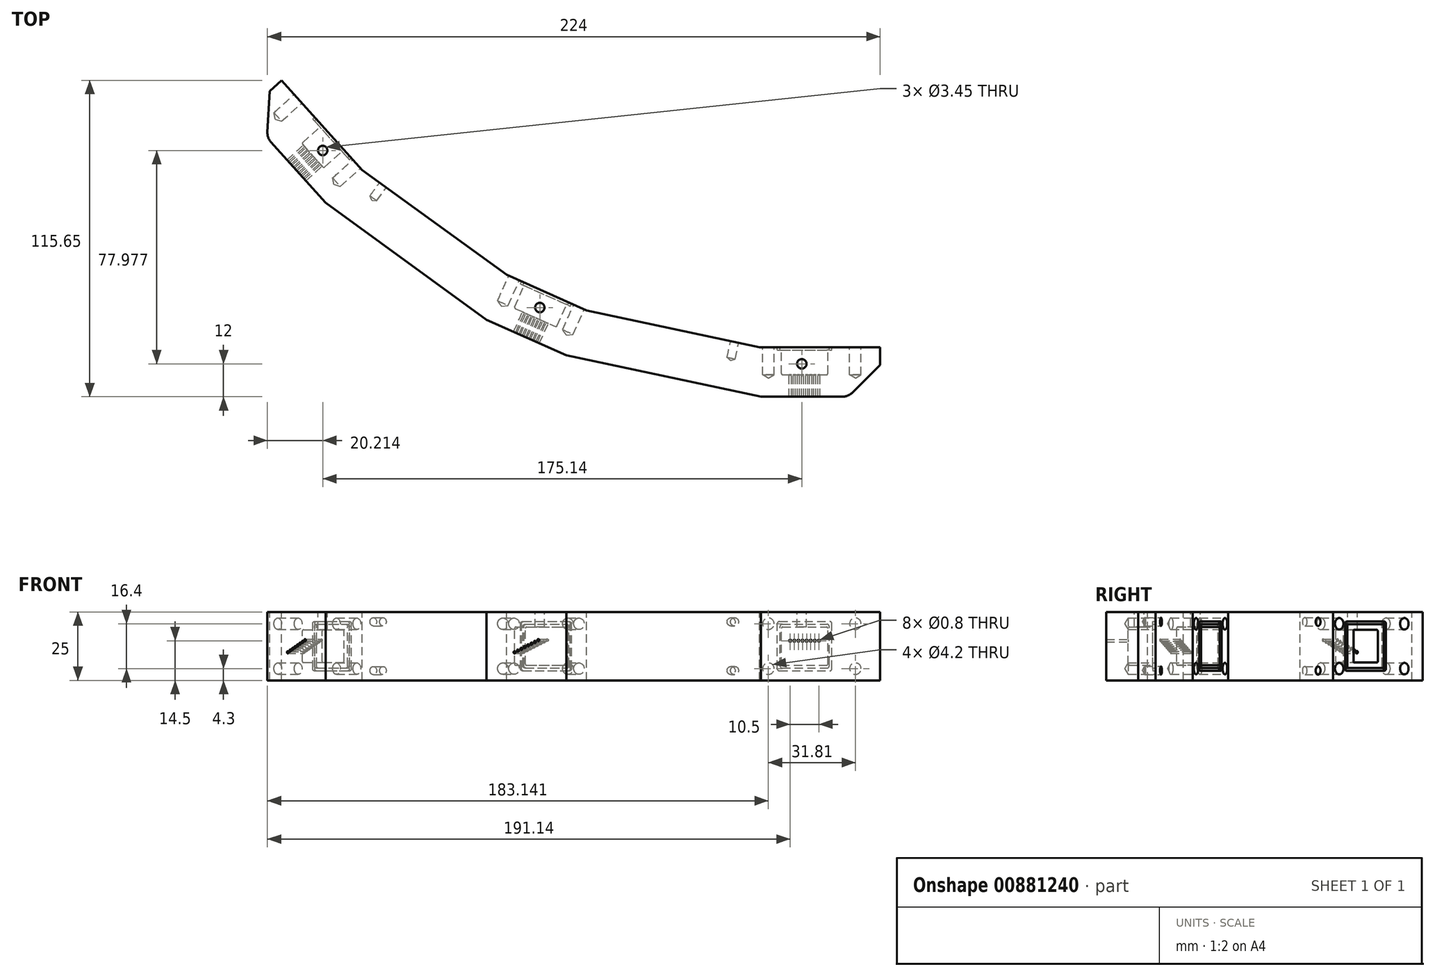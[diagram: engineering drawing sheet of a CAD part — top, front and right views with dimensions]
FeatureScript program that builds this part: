
annotation { "Feature Type Name" : "Feature", "Feature Type Description" : "" }
export const myFeature = defineFeature(function(context is Context, id is Id, definition is map)
    precondition{}
    {
        {
            var Q0;
            Q0=qCreatedBy(makeId("Top.planeOp"),FACE);
            var sketch = newSketch(context, id + "F0", { "sketchPlane" : qUnion([Q0])});
            skCircle(sketch, "E0", {"center": v(0, -260) * mm, "radius": 6 * mm});
            skCircle(sketch, "E1", {"center": v(-105.75, -237.52) * mm, "radius": 6 * mm});
            skCircle(sketch, "E2", {"center": v(-193.22, -173.97) * mm, "radius": 6 * mm});
            skPoint(sketch, "E3", {"position": v(-185.79, -167.28) * mm});
            skPoint(sketch, "E4", {"position": v(-101.68, -228.39) * mm});
            skPoint(sketch, "E5", {"position": v(0, -250) * mm});
            skLineSegment(sketch, "E6.trimOffspring", {"start": v(-103.31, -232.04) * mm, "end": v(-105.75, -237.52) * mm});
            skLineSegment(sketch, "E7.trimOffspring", {"start": v(0, -254) * mm, "end": v(0, -260) * mm});
            skLineSegment(sketch, "E8.trimOffspring", {"start": v(-188.76, -169.96) * mm, "end": v(-193.22, -173.97) * mm});
            skLineSegment(sketch, "E9", {"start": v(-185.79, -167.28) * mm, "end": v(-175.08, -179.17) * mm});
            skLineSegment(sketch, "E10", {"start": v(-185.79, -167.28) * mm, "end": v(-195.1, -156.93) * mm});
            skLineSegment(sketch, "E11", {"start": v(-101.68, -228.39) * mm, "end": v(-116.3, -221.88) * mm});
            skLineSegment(sketch, "E12", {"start": v(-101.68, -228.39) * mm, "end": v(-87.07, -234.9) * mm});
            skLineSegment(sketch, "E13", {"start": v(0, -250) * mm, "end": v(-16, -250) * mm});
            skLineSegment(sketch, "E14", {"start": v(0, -250) * mm, "end": v(13.93, -250) * mm});
            skLineSegment(sketch, "E15", {"start": v(-175.08, -179.17) * mm, "end": v(-116.3, -221.88) * mm});
            skLineSegment(sketch, "E16", {"start": v(-87.07, -234.9) * mm, "end": v(-16, -250) * mm});
            skLineSegment(sketch, "E17", {"start": v(-196.38, -153.32) * mm, "end": v(-195.6, -138.3) * mm});
            skLineSegment(sketch, "E18", {"start": v(17.46, -248.54) * mm, "end": v(27.61, -238.39) * mm});
            skPoint(sketch, "E19", {"position": v(-196.5, -155.4) * mm});
            skPoint(sketch, "E20", {"position": v(-172.4, -155.24) * mm});
            skLineSegment(sketch, "E21", {"start": v(-172.4, -155.24) * mm, "end": v(-191.22, -134.35) * mm});
            skLineSegment(sketch, "E22", {"start": v(-195.6, -138.3) * mm, "end": v(-191.22, -134.35) * mm});
            skPoint(sketch, "E23", {"position": v(-94.36, -211.94) * mm});
            skLineSegment(sketch, "E24", {"start": v(-94.36, -211.94) * mm, "end": v(-108.98, -205.43) * mm});
            skLineSegment(sketch, "E25", {"start": v(-172.4, -155.24) * mm, "end": v(-161.7, -167.13) * mm});
            skLineSegment(sketch, "E26", {"start": v(-161.7, -167.13) * mm, "end": v(-108.98, -205.43) * mm});
            skLineSegment(sketch, "E27", {"start": v(-94.36, -211.94) * mm, "end": v(-79.75, -218.45) * mm});
            skPoint(sketch, "E28", {"position": v(-0.5, -232) * mm});
            skLineSegment(sketch, "E29", {"start": v(-0.5, -232) * mm, "end": v(27.61, -232) * mm});
            skLineSegment(sketch, "E30", {"start": v(27.61, -238.39) * mm, "end": v(27.61, -232) * mm});
            skLineSegment(sketch, "E31", {"start": v(-0.5, -232) * mm, "end": v(-16.5, -232) * mm});
            skLineSegment(sketch, "E32", {"start": v(-79.75, -218.45) * mm, "end": v(-16.5, -232) * mm});
            skPoint(sketch, "E33.start.orphan", {"position": v(0, 0) * mm});
            skArc(sketch, "E34.filletArc", {"start": v(-196.38, -153.32) * mm, "mid": v(-196.1, -155.25) * mm, "end": v(-195.1, -156.93) * mm});
            skPoint(sketch, "E35.visualSharp", {"position": v(16, -250) * mm});
            skArc(sketch, "E35.filletArc", {"start": v(13.93, -250) * mm, "mid": v(15.84, -249.62) * mm, "end": v(17.46, -248.54) * mm});
            skSolve(sketch);
        }
        {
            var Q0;
            Q0=makeQuery(id+"F0.imprint","IMPRINT",FACE,{"disambiguationData":[TD([[makeQuery(id+"F0.imprint","IMPRINT",EDGE,{"derivedFrom":sQuery(id+"F0.wireOp",EDGE,"E9")}),1.0]])]});
            extrude(context, id + "F1", {"entities" : qUnion([Q0]), "oppositeDirection" : true, "depth" : 25 * mm, "offsetDistance" : 25 * mm});
        }
        {
            var Q0;
            Q0=makeQuery(id+"F1.opExtrude","SWEPT_FACE",FACE,{"disambiguationData":[OSD([sQuery(id+"F0.wireOp",EDGE,"E24"),sQuery(id+"F0.wireOp",EDGE,"E27")])]});
            var sketch = newSketch(context, id + "F2", { "sketchPlane" : qUnion([Q0])});
            skPoint(sketch, "E36", {"position": v(0, -12.5) * mm});
            skLineSegment(sketch, "E37.bottom", {"start": v(8.5, -19.5) * mm, "end": v(-8.5, -19.5) * mm});
            skLineSegment(sketch, "E37.top", {"start": v(8.5, -5.5) * mm, "end": v(-8.5, -5.5) * mm});
            skLineSegment(sketch, "E37.left", {"start": v(8.5, -19.5) * mm, "end": v(8.5, -5.5) * mm});
            skLineSegment(sketch, "E37.right", {"start": v(-8.5, -19.5) * mm, "end": v(-8.5, -5.5) * mm});
            skSolve(sketch);
        }
        {
            var Q0;
            Q0=makeQuery(id+"F2.imprint","IMPRINT",FACE,{"disambiguationData":[TD([[makeQuery(id+"F2.imprint","IMPRINT",EDGE,{"derivedFrom":sQuery(id+"F2.wireOp",EDGE,"E37.bottom")}),-1.0]])]});
            extrude(context, id + "F3", {"entities" : qUnion([Q0]), "operationType" : NewBodyOperationType.REMOVE, "oppositeDirection" : true, "depth" : 10 * mm, "offsetDistance" : 25 * mm});
        }
        {
            var Q0;
            Q0=makeQuery(id+"F1.opExtrude","SWEPT_FACE",FACE,{"disambiguationData":[OSD([sQuery(id+"F0.wireOp",EDGE,"E21"),sQuery(id+"F0.wireOp",EDGE,"E25")])]});
            var sketch = newSketch(context, id + "F4", { "sketchPlane" : qUnion([Q0])});
            skPoint(sketch, "E38.middle", {"position": v(0, -12.5) * mm});
            skLineSegment(sketch, "E39.bottom", {"start": v(6, -18.5) * mm, "end": v(-6, -18.5) * mm});
            skLineSegment(sketch, "E39.top", {"start": v(6, -6.5) * mm, "end": v(-6, -6.5) * mm});
            skLineSegment(sketch, "E39.left", {"start": v(6, -18.5) * mm, "end": v(6, -6.5) * mm});
            skLineSegment(sketch, "E39.right", {"start": v(-6, -18.5) * mm, "end": v(-6, -6.5) * mm});
            skSolve(sketch);
        }
        {
            var Q0;
            Q0=makeQuery(id+"F4.imprint","IMPRINT",FACE,{"disambiguationData":[TD([[makeQuery(id+"F4.imprint","IMPRINT",EDGE,{"derivedFrom":sQuery(id+"F4.wireOp",EDGE,"E39.bottom")}),-1.0]])]});
            extrude(context, id + "F5", {"entities" : qUnion([Q0]), "operationType" : NewBodyOperationType.REMOVE, "oppositeDirection" : true, "depth" : 10 * mm, "offsetDistance" : 25 * mm});
        }
        {
            var Q0;
            Q0=makeQuery(id+"F5.boolean.opBoolean","COPY",FACE,{"derivedFrom":makeQuery(id+"F5.opExtrude","CAP_FACE",FACE,{"disambiguationData":[OSD([sQuery(id+"F4.wireOp",EDGE,"E39.bottom"),sQuery(id+"F4.wireOp",EDGE,"E39.top"),sQuery(id+"F4.wireOp",EDGE,"E39.left"),sQuery(id+"F4.wireOp",EDGE,"E39.right")])],"isStart":false})});
            var sketch = newSketch(context, id + "F6", { "sketchPlane" : qUnion([Q0])});
            skLineSegment(sketch, "E40", {"start": v(0, -18.5) * mm, "end": v(0, -12.5) * mm});
            skLineSegment(sketch, "E41", {"start": v(0, -12.5) * mm, "end": v(6.8, -15.67) * mm});
            skLineSegment(sketch, "E42", {"start": v(0, -12.5) * mm, "end": v(-6.8, -9.33) * mm});
            skPoint(sketch, "E43", {"position": v(0.68, -12.82) * mm});
            skPoint(sketch, "E44", {"position": v(2.04, -13.45) * mm});
            skPoint(sketch, "E45", {"position": v(3.4, -14.08) * mm});
            skPoint(sketch, "E46", {"position": v(4.76, -14.72) * mm});
            skPoint(sketch, "E47", {"position": v(-0.68, -12.18) * mm});
            skPoint(sketch, "E48", {"position": v(-2.04, -11.55) * mm});
            skPoint(sketch, "E49", {"position": v(-3.4, -10.92) * mm});
            skPoint(sketch, "E50", {"position": v(-4.76, -10.28) * mm});
            skSolve(sketch);
        }
        {
            var Q0;
            Q0=sQuery(id+"F6.wireOp",VERTEX,"E46");
            var Q1;
            Q1=sQuery(id+"F6.wireOp",VERTEX,"E45");
            var Q2;
            Q2=sQuery(id+"F6.wireOp",VERTEX,"E44");
            var Q3;
            Q3=sQuery(id+"F6.wireOp",VERTEX,"E43");
            var Q4;
            Q4=sQuery(id+"F6.wireOp",VERTEX,"E47");
            var Q5;
            Q5=sQuery(id+"F6.wireOp",VERTEX,"E48");
            var Q6;
            Q6=sQuery(id+"F6.wireOp",VERTEX,"E49");
            var Q7;
            Q7=sQuery(id+"F6.wireOp",VERTEX,"E50");
            var Q8;
            Q8=makeQuery(id+"F1.opExtrude","SWEPT_BODY",BODY,{"disambiguationData":[OSD([sQuery(id+"F0.wireOp",EDGE,"E9"),sQuery(id+"F0.wireOp",EDGE,"E10"),sQuery(id+"F0.wireOp",EDGE,"E11"),sQuery(id+"F0.wireOp",EDGE,"E12"),sQuery(id+"F0.wireOp",EDGE,"E13"),sQuery(id+"F0.wireOp",EDGE,"E14"),sQuery(id+"F0.wireOp",EDGE,"E15"),sQuery(id+"F0.wireOp",EDGE,"E16"),sQuery(id+"F0.wireOp",EDGE,"E17"),sQuery(id+"F0.wireOp",EDGE,"E18"),sQuery(id+"F0.wireOp",EDGE,"E21"),sQuery(id+"F0.wireOp",EDGE,"E22"),sQuery(id+"F0.wireOp",EDGE,"E24"),sQuery(id+"F0.wireOp",EDGE,"E25"),sQuery(id+"F0.wireOp",EDGE,"E26"),sQuery(id+"F0.wireOp",EDGE,"E27"),sQuery(id+"F0.wireOp",EDGE,"E29"),sQuery(id+"F0.wireOp",EDGE,"E30"),sQuery(id+"F0.wireOp",EDGE,"E31"),sQuery(id+"F0.wireOp",EDGE,"E32"),sQuery(id+"F0.wireOp",EDGE,"E34.filletArc"),sQuery(id+"F0.wireOp",EDGE,"E35.filletArc")])]});
            hole(context, id + "F7", {"style" : HoleStyle.C_SINK, "endStyle" : HoleEndStyle.THROUGH, "holeDiameter" : 0.8 * mm, "cSinkDiameter" : 0.87 * mm, "cSinkAngle" : 60 * degree, "majorDiameter" : 5 * mm, "isTappedThrough" : true, "tappedDepth" : 12 * mm, "tapClearance" : 3, "locations" : qUnion([Q0, Q1, Q2, Q3, Q4, Q5, Q6, Q7]), "scope" : qUnion([Q8])});
        }
        {
            var Q0;
            Q0=makeQuery(id+"F3.boolean.opBoolean","COPY",FACE,{"derivedFrom":makeQuery(id+"F3.opExtrude","CAP_FACE",FACE,{"disambiguationData":[OSD([sQuery(id+"F2.wireOp",EDGE,"E37.bottom"),sQuery(id+"F2.wireOp",EDGE,"E37.top"),sQuery(id+"F2.wireOp",EDGE,"E37.left"),sQuery(id+"F2.wireOp",EDGE,"E37.right")])],"isStart":false})});
            var sketch = newSketch(context, id + "F8", { "sketchPlane" : qUnion([Q0])});
            skLineSegment(sketch, "E51", {"start": v(0, -19.5) * mm, "end": v(0, -12.5) * mm});
            skLineSegment(sketch, "E52", {"start": v(0, -12.5) * mm, "end": v(5.15, -14.9) * mm});
            skLineSegment(sketch, "E53", {"start": v(0, -12.5) * mm, "end": v(-6.8, -9.33) * mm});
            skPoint(sketch, "E54", {"position": v(0.68, -12.82) * mm});
            skPoint(sketch, "E55", {"position": v(2.04, -13.45) * mm});
            skPoint(sketch, "E56", {"position": v(3.4, -14.08) * mm});
            skPoint(sketch, "E57", {"position": v(-0.68, -12.18) * mm});
            skPoint(sketch, "E58", {"position": v(-2.04, -11.55) * mm});
            skPoint(sketch, "E59", {"position": v(-3.4, -10.92) * mm});
            skPoint(sketch, "E60", {"position": v(4.76, -14.72) * mm});
            skPoint(sketch, "E61", {"position": v(-4.76, -10.28) * mm});
            skSolve(sketch);
        }
        {
            var Q0;
            Q0=sQuery(id+"F8.wireOp",VERTEX,"E60");
            var Q1;
            Q1=sQuery(id+"F8.wireOp",VERTEX,"E56");
            var Q2;
            Q2=sQuery(id+"F8.wireOp",VERTEX,"E55");
            var Q3;
            Q3=sQuery(id+"F8.wireOp",VERTEX,"E54");
            var Q4;
            Q4=sQuery(id+"F8.wireOp",VERTEX,"E57");
            var Q5;
            Q5=sQuery(id+"F8.wireOp",VERTEX,"E58");
            var Q6;
            Q6=sQuery(id+"F8.wireOp",VERTEX,"E59");
            var Q7;
            Q7=sQuery(id+"F8.wireOp",VERTEX,"E61");
            var Q8;
            Q8=makeQuery(id+"F1.opExtrude","SWEPT_BODY",BODY,{"disambiguationData":[OSD([sQuery(id+"F0.wireOp",EDGE,"E9"),sQuery(id+"F0.wireOp",EDGE,"E10"),sQuery(id+"F0.wireOp",EDGE,"E11"),sQuery(id+"F0.wireOp",EDGE,"E12"),sQuery(id+"F0.wireOp",EDGE,"E13"),sQuery(id+"F0.wireOp",EDGE,"E14"),sQuery(id+"F0.wireOp",EDGE,"E15"),sQuery(id+"F0.wireOp",EDGE,"E16"),sQuery(id+"F0.wireOp",EDGE,"E17"),sQuery(id+"F0.wireOp",EDGE,"E18"),sQuery(id+"F0.wireOp",EDGE,"E21"),sQuery(id+"F0.wireOp",EDGE,"E22"),sQuery(id+"F0.wireOp",EDGE,"E24"),sQuery(id+"F0.wireOp",EDGE,"E25"),sQuery(id+"F0.wireOp",EDGE,"E26"),sQuery(id+"F0.wireOp",EDGE,"E27"),sQuery(id+"F0.wireOp",EDGE,"E29"),sQuery(id+"F0.wireOp",EDGE,"E30"),sQuery(id+"F0.wireOp",EDGE,"E31"),sQuery(id+"F0.wireOp",EDGE,"E32"),sQuery(id+"F0.wireOp",EDGE,"E34.filletArc"),sQuery(id+"F0.wireOp",EDGE,"E35.filletArc")])]});
            hole(context, id + "F9", {"style" : HoleStyle.C_SINK, "endStyle" : HoleEndStyle.THROUGH, "holeDiameter" : 0.8 * mm, "cSinkDiameter" : 0.87 * mm, "cSinkAngle" : 60 * degree, "majorDiameter" : 5 * mm, "isTappedThrough" : true, "tappedDepth" : 12 * mm, "tapClearance" : 3, "locations" : qUnion([Q0, Q1, Q2, Q3, Q4, Q5, Q6, Q7]), "scope" : qUnion([Q8])});
        }
        {
            var Q0;
            Q0=makeQuery(id+"F1.opExtrude","SWEPT_FACE",FACE,{"disambiguationData":[OSD([sQuery(id+"F0.wireOp",EDGE,"E29"),sQuery(id+"F0.wireOp",EDGE,"E31")])]});
            var sketch = newSketch(context, id + "F10", { "sketchPlane" : qUnion([Q0])});
            skLineSegment(sketch, "E62.bottom", {"start": v(8.5, -19.5) * mm, "end": v(-8.5, -19.5) * mm});
            skLineSegment(sketch, "E62.top", {"start": v(8.5, -5.5) * mm, "end": v(-8.5, -5.5) * mm});
            skLineSegment(sketch, "E62.left", {"start": v(8.5, -19.5) * mm, "end": v(8.5, -5.5) * mm});
            skLineSegment(sketch, "E62.right", {"start": v(-8.5, -19.5) * mm, "end": v(-8.5, -5.5) * mm});
            skPoint(sketch, "E62.middle", {"position": v(0, -12.5) * mm});
            skSolve(sketch);
        }
        {
            var Q0;
            Q0=makeQuery(id+"F10.imprint","IMPRINT",FACE,{"disambiguationData":[TD([[makeQuery(id+"F10.imprint","IMPRINT",EDGE,{"derivedFrom":sQuery(id+"F10.wireOp",EDGE,"E62.bottom")}),-1.0]])]});
            extrude(context, id + "F11", {"entities" : qUnion([Q0]), "operationType" : NewBodyOperationType.REMOVE, "oppositeDirection" : true, "depth" : 10 * mm, "offsetDistance" : 25 * mm});
        }
        {
            var Q0;
            Q0=makeQuery(id+"F11.boolean.opBoolean","COPY",FACE,{"derivedFrom":makeQuery(id+"F11.opExtrude","CAP_FACE",FACE,{"disambiguationData":[OSD([sQuery(id+"F10.wireOp",EDGE,"E62.bottom"),sQuery(id+"F10.wireOp",EDGE,"E62.top"),sQuery(id+"F10.wireOp",EDGE,"E62.left"),sQuery(id+"F10.wireOp",EDGE,"E62.right")])],"isStart":false})});
            var sketch = newSketch(context, id + "F12", { "sketchPlane" : qUnion([Q0])});
            skLineSegment(sketch, "E63", {"start": v(0, -19.5) * mm, "end": v(0, -10.5) * mm});
            skPoint(sketch, "E64", {"position": v(0.75, -10.5) * mm});
            skPoint(sketch, "E65", {"position": v(2.25, -10.5) * mm});
            skPoint(sketch, "E66", {"position": v(3.75, -10.5) * mm});
            skPoint(sketch, "E67", {"position": v(5.25, -10.5) * mm});
            skPoint(sketch, "E68", {"position": v(-0.75, -10.5) * mm});
            skPoint(sketch, "E69", {"position": v(-2.25, -10.5) * mm});
            skPoint(sketch, "E70", {"position": v(-3.75, -10.5) * mm});
            skPoint(sketch, "E71", {"position": v(-5.25, -10.5) * mm});
            skSolve(sketch);
        }
        {
            var Q0;
            Q0=sQuery(id+"F12.wireOp",VERTEX,"E67");
            var Q1;
            Q1=sQuery(id+"F12.wireOp",VERTEX,"E66");
            var Q2;
            Q2=sQuery(id+"F12.wireOp",VERTEX,"E65");
            var Q3;
            Q3=sQuery(id+"F12.wireOp",VERTEX,"E64");
            var Q4;
            Q4=sQuery(id+"F12.wireOp",VERTEX,"E68");
            var Q5;
            Q5=sQuery(id+"F12.wireOp",VERTEX,"E69");
            var Q6;
            Q6=sQuery(id+"F12.wireOp",VERTEX,"E70");
            var Q7;
            Q7=sQuery(id+"F12.wireOp",VERTEX,"E71");
            var Q8;
            Q8=makeQuery(id+"F1.opExtrude","SWEPT_BODY",BODY,{"disambiguationData":[OSD([sQuery(id+"F0.wireOp",EDGE,"E9"),sQuery(id+"F0.wireOp",EDGE,"E10"),sQuery(id+"F0.wireOp",EDGE,"E11"),sQuery(id+"F0.wireOp",EDGE,"E12"),sQuery(id+"F0.wireOp",EDGE,"E13"),sQuery(id+"F0.wireOp",EDGE,"E14"),sQuery(id+"F0.wireOp",EDGE,"E15"),sQuery(id+"F0.wireOp",EDGE,"E16"),sQuery(id+"F0.wireOp",EDGE,"E17"),sQuery(id+"F0.wireOp",EDGE,"E18"),sQuery(id+"F0.wireOp",EDGE,"E21"),sQuery(id+"F0.wireOp",EDGE,"E22"),sQuery(id+"F0.wireOp",EDGE,"E24"),sQuery(id+"F0.wireOp",EDGE,"E25"),sQuery(id+"F0.wireOp",EDGE,"E26"),sQuery(id+"F0.wireOp",EDGE,"E27"),sQuery(id+"F0.wireOp",EDGE,"E29"),sQuery(id+"F0.wireOp",EDGE,"E30"),sQuery(id+"F0.wireOp",EDGE,"E31"),sQuery(id+"F0.wireOp",EDGE,"E32"),sQuery(id+"F0.wireOp",EDGE,"E34.filletArc"),sQuery(id+"F0.wireOp",EDGE,"E35.filletArc")])]});
            hole(context, id + "F13", {"style" : HoleStyle.C_SINK, "endStyle" : HoleEndStyle.THROUGH, "holeDiameter" : 0.8 * mm, "cSinkDiameter" : 0.87 * mm, "cSinkAngle" : 60 * degree, "majorDiameter" : 5 * mm, "isTappedThrough" : true, "tappedDepth" : 12 * mm, "tapClearance" : 3, "locations" : qUnion([Q0, Q1, Q2, Q3, Q4, Q5, Q6, Q7]), "scope" : qUnion([Q8])});
        }
        {
            var Q0;
            Q0=makeQuery(id+"F1.opExtrude","SWEPT_FACE",FACE,{"disambiguationData":[OSD([sQuery(id+"F0.wireOp",EDGE,"E24"),sQuery(id+"F0.wireOp",EDGE,"E27")])]});
            var sketch = newSketch(context, id + "F14", { "sketchPlane" : qUnion([Q0])});
            skPoint(sketch, "E72", {"position": v(-8.5, -12.5) * mm});
            skPoint(sketch, "E73", {"position": v(8.5, -12.5) * mm});
            skLineSegment(sketch, "E74", {"start": v(-8.5, -12.5) * mm, "end": v(8.5, -12.5) * mm});
            skLineSegment(sketch, "E75.bottom", {"start": v(8.2, -20.5) * mm, "end": v(-8.2, -20.5) * mm});
            skLineSegment(sketch, "E75.top", {"start": v(8.2, -4.5) * mm, "end": v(-8.2, -4.5) * mm});
            skLineSegment(sketch, "E75.left", {"start": v(9, -19.7) * mm, "end": v(9, -5.3) * mm});
            skLineSegment(sketch, "E75.right", {"start": v(-9, -19.7) * mm, "end": v(-9, -5.3) * mm});
            skPoint(sketch, "E75.middle", {"position": v(0, -12.5) * mm});
            skLineSegment(sketch, "E76.bottom", {"start": v(9.2, -21.5) * mm, "end": v(-9.2, -21.5) * mm});
            skLineSegment(sketch, "E76.top", {"start": v(9.2, -3.5) * mm, "end": v(-9.2, -3.5) * mm});
            skLineSegment(sketch, "E76.left", {"start": v(10, -20.7) * mm, "end": v(10, -4.3) * mm});
            skLineSegment(sketch, "E76.right", {"start": v(-10, -20.7) * mm, "end": v(-10, -4.3) * mm});
            skPoint(sketch, "E77.visualSharp", {"position": v(-9, -4.5) * mm});
            skArc(sketch, "E77.filletArc", {"start": v(-8.2, -4.5) * mm, "mid": v(-8.77, -4.73) * mm, "end": v(-9, -5.3) * mm});
            skPoint(sketch, "E78.visualSharp", {"position": v(-10, -3.5) * mm});
            skArc(sketch, "E78.filletArc", {"start": v(-9.2, -3.5) * mm, "mid": v(-9.77, -3.73) * mm, "end": v(-10, -4.3) * mm});
            skPoint(sketch, "E79.visualSharp", {"position": v(10, -3.5) * mm});
            skArc(sketch, "E79.filletArc", {"start": v(10, -4.3) * mm, "mid": v(9.77, -3.73) * mm, "end": v(9.2, -3.5) * mm});
            skPoint(sketch, "E80.visualSharp", {"position": v(9, -4.5) * mm});
            skArc(sketch, "E80.filletArc", {"start": v(9, -5.3) * mm, "mid": v(8.77, -4.73) * mm, "end": v(8.2, -4.5) * mm});
            skPoint(sketch, "E81.visualSharp", {"position": v(10, -21.5) * mm});
            skArc(sketch, "E81.filletArc", {"start": v(9.2, -21.5) * mm, "mid": v(9.77, -21.27) * mm, "end": v(10, -20.7) * mm});
            skPoint(sketch, "E82.visualSharp", {"position": v(9, -20.5) * mm});
            skArc(sketch, "E82.filletArc", {"start": v(8.2, -20.5) * mm, "mid": v(8.77, -20.27) * mm, "end": v(9, -19.7) * mm});
            skPoint(sketch, "E83.visualSharp", {"position": v(-9, -20.5) * mm});
            skArc(sketch, "E83.filletArc", {"start": v(-9, -19.7) * mm, "mid": v(-8.77, -20.27) * mm, "end": v(-8.2, -20.5) * mm});
            skPoint(sketch, "E84.visualSharp", {"position": v(-10, -21.5) * mm});
            skArc(sketch, "E84.filletArc", {"start": v(-10, -20.7) * mm, "mid": v(-9.77, -21.27) * mm, "end": v(-9.2, -21.5) * mm});
            skSolve(sketch);
        }
        {
            var Q0;
            Q0=makeQuery(id+"F14.imprint","IMPRINT",FACE,{"disambiguationData":[TD([[makeQuery(id+"F14.imprint","IMPRINT",EDGE,{"derivedFrom":sQuery(id+"F14.wireOp",EDGE,"E75.bottom")}),1.0]])]});
            extrude(context, id + "F15", {"entities" : qUnion([Q0]), "operationType" : NewBodyOperationType.REMOVE, "oppositeDirection" : true, "depth" : 1 * mm, "offsetDistance" : 25 * mm});
        }
        {
            var Q0;
            Q0=makeQuery(id+"F1.opExtrude","SWEPT_FACE",FACE,{"disambiguationData":[OSD([sQuery(id+"F0.wireOp",EDGE,"E21"),sQuery(id+"F0.wireOp",EDGE,"E25")])]});
            var sketch = newSketch(context, id + "F16", { "sketchPlane" : qUnion([Q0])});
            skLineSegment(sketch, "E85", {"start": v(-6, -12.5) * mm, "end": v(6, -12.5) * mm});
            skLineSegment(sketch, "E86.bottom", {"start": v(8.2, -20.5) * mm, "end": v(-8.2, -20.5) * mm});
            skLineSegment(sketch, "E86.top", {"start": v(8.2, -4.5) * mm, "end": v(-8.2, -4.5) * mm});
            skLineSegment(sketch, "E86.left", {"start": v(9, -19.7) * mm, "end": v(9, -5.3) * mm});
            skLineSegment(sketch, "E86.right", {"start": v(-9, -19.7) * mm, "end": v(-9, -5.3) * mm});
            skPoint(sketch, "E86.middle", {"position": v(0, -12.5) * mm});
            skLineSegment(sketch, "E87.bottom", {"start": v(9.2, -21.5) * mm, "end": v(-9.2, -21.5) * mm});
            skLineSegment(sketch, "E87.top", {"start": v(9.2, -3.5) * mm, "end": v(-9.2, -3.5) * mm});
            skLineSegment(sketch, "E87.left", {"start": v(10, -20.7) * mm, "end": v(10, -4.3) * mm});
            skLineSegment(sketch, "E87.right", {"start": v(-10, -20.7) * mm, "end": v(-10, -4.3) * mm});
            skPoint(sketch, "E88.visualSharp", {"position": v(-9, -4.5) * mm});
            skArc(sketch, "E88.filletArc", {"start": v(-8.2, -4.5) * mm, "mid": v(-8.77, -4.73) * mm, "end": v(-9, -5.3) * mm});
            skPoint(sketch, "E89.visualSharp", {"position": v(-10, -3.5) * mm});
            skArc(sketch, "E89.filletArc", {"start": v(-9.2, -3.5) * mm, "mid": v(-9.77, -3.73) * mm, "end": v(-10, -4.3) * mm});
            skPoint(sketch, "E90.visualSharp", {"position": v(10, -3.5) * mm});
            skArc(sketch, "E90.filletArc", {"start": v(10, -4.3) * mm, "mid": v(9.77, -3.73) * mm, "end": v(9.2, -3.5) * mm});
            skPoint(sketch, "E91.visualSharp", {"position": v(9, -4.5) * mm});
            skArc(sketch, "E91.filletArc", {"start": v(9, -5.3) * mm, "mid": v(8.77, -4.73) * mm, "end": v(8.2, -4.5) * mm});
            skPoint(sketch, "E92.visualSharp", {"position": v(10, -21.5) * mm});
            skArc(sketch, "E92.filletArc", {"start": v(9.2, -21.5) * mm, "mid": v(9.77, -21.27) * mm, "end": v(10, -20.7) * mm});
            skPoint(sketch, "E93.visualSharp", {"position": v(9, -20.5) * mm});
            skArc(sketch, "E93.filletArc", {"start": v(8.2, -20.5) * mm, "mid": v(8.77, -20.27) * mm, "end": v(9, -19.7) * mm});
            skPoint(sketch, "E94.visualSharp", {"position": v(-9, -20.5) * mm});
            skArc(sketch, "E94.filletArc", {"start": v(-9, -19.7) * mm, "mid": v(-8.77, -20.27) * mm, "end": v(-8.2, -20.5) * mm});
            skPoint(sketch, "E95.visualSharp", {"position": v(-10, -21.5) * mm});
            skArc(sketch, "E95.filletArc", {"start": v(-10, -20.7) * mm, "mid": v(-9.77, -21.27) * mm, "end": v(-9.2, -21.5) * mm});
            skSolve(sketch);
        }
        {
            var Q0;
            Q0=makeQuery(id+"F16.imprint","IMPRINT",FACE,{"disambiguationData":[TD([[makeQuery(id+"F16.imprint","IMPRINT",EDGE,{"derivedFrom":sQuery(id+"F16.wireOp",EDGE,"E86.bottom")}),1.0]])]});
            extrude(context, id + "F17", {"entities" : qUnion([Q0]), "operationType" : NewBodyOperationType.REMOVE, "oppositeDirection" : true, "depth" : 1 * mm, "offsetDistance" : 25 * mm});
        }
        {
            var Q0;
            Q0=makeQuery(id+"F1.opExtrude","SWEPT_FACE",FACE,{"disambiguationData":[OSD([sQuery(id+"F0.wireOp",EDGE,"E29"),sQuery(id+"F0.wireOp",EDGE,"E31")])]});
            var sketch = newSketch(context, id + "F18", { "sketchPlane" : qUnion([Q0])});
            skLineSegment(sketch, "E96", {"start": v(-8.5, -12.5) * mm, "end": v(8.5, -12.5) * mm});
            skLineSegment(sketch, "E97.bottom", {"start": v(8.2, -20.5) * mm, "end": v(-8.2, -20.5) * mm});
            skLineSegment(sketch, "E97.top", {"start": v(8.2, -4.5) * mm, "end": v(-8.2, -4.5) * mm});
            skLineSegment(sketch, "E97.left", {"start": v(9, -19.7) * mm, "end": v(9, -5.3) * mm});
            skLineSegment(sketch, "E97.right", {"start": v(-9, -19.7) * mm, "end": v(-9, -5.3) * mm});
            skPoint(sketch, "E97.middle", {"position": v(0, -12.5) * mm});
            skLineSegment(sketch, "E98.bottom", {"start": v(9.2, -21.5) * mm, "end": v(-9.2, -21.5) * mm});
            skLineSegment(sketch, "E98.top", {"start": v(9.2, -3.5) * mm, "end": v(-9.2, -3.5) * mm});
            skLineSegment(sketch, "E98.left", {"start": v(10, -20.7) * mm, "end": v(10, -4.3) * mm});
            skLineSegment(sketch, "E98.right", {"start": v(-10, -20.7) * mm, "end": v(-10, -4.3) * mm});
            skPoint(sketch, "E99.visualSharp", {"position": v(-9, -4.5) * mm});
            skArc(sketch, "E99.filletArc", {"start": v(-8.2, -4.5) * mm, "mid": v(-8.77, -4.73) * mm, "end": v(-9, -5.3) * mm});
            skPoint(sketch, "E100.visualSharp", {"position": v(-10, -3.5) * mm});
            skArc(sketch, "E100.filletArc", {"start": v(-9.2, -3.5) * mm, "mid": v(-9.77, -3.73) * mm, "end": v(-10, -4.3) * mm});
            skPoint(sketch, "E101.visualSharp", {"position": v(10, -3.5) * mm});
            skArc(sketch, "E101.filletArc", {"start": v(10, -4.3) * mm, "mid": v(9.77, -3.73) * mm, "end": v(9.2, -3.5) * mm});
            skPoint(sketch, "E102.visualSharp", {"position": v(9, -4.5) * mm});
            skArc(sketch, "E102.filletArc", {"start": v(9, -5.3) * mm, "mid": v(8.77, -4.73) * mm, "end": v(8.2, -4.5) * mm});
            skPoint(sketch, "E103.visualSharp", {"position": v(9, -20.5) * mm});
            skArc(sketch, "E103.filletArc", {"start": v(8.2, -20.5) * mm, "mid": v(8.77, -20.27) * mm, "end": v(9, -19.7) * mm});
            skPoint(sketch, "E104.visualSharp", {"position": v(10, -21.5) * mm});
            skArc(sketch, "E104.filletArc", {"start": v(9.2, -21.5) * mm, "mid": v(9.77, -21.27) * mm, "end": v(10, -20.7) * mm});
            skPoint(sketch, "E105.visualSharp", {"position": v(-10, -21.5) * mm});
            skArc(sketch, "E105.filletArc", {"start": v(-10, -20.7) * mm, "mid": v(-9.77, -21.27) * mm, "end": v(-9.2, -21.5) * mm});
            skPoint(sketch, "E106.visualSharp", {"position": v(-9, -20.5) * mm});
            skArc(sketch, "E106.filletArc", {"start": v(-9, -19.7) * mm, "mid": v(-8.77, -20.27) * mm, "end": v(-8.2, -20.5) * mm});
            skSolve(sketch);
        }
        {
            var Q0;
            Q0=makeQuery(id+"F18.imprint","IMPRINT",FACE,{"disambiguationData":[TD([[makeQuery(id+"F18.imprint","IMPRINT",EDGE,{"derivedFrom":sQuery(id+"F18.wireOp",EDGE,"E97.bottom")}),1.0]])]});
            extrude(context, id + "F19", {"entities" : qUnion([Q0]), "operationType" : NewBodyOperationType.REMOVE, "oppositeDirection" : true, "depth" : 1 * mm, "offsetDistance" : 25 * mm});
        }
        {
            var Q0;
            Q0=makeQuery(id+"F1.opExtrude","CAP_FACE",FACE,{"disambiguationData":[OSD([sQuery(id+"F0.wireOp",EDGE,"E9"),sQuery(id+"F0.wireOp",EDGE,"E10"),sQuery(id+"F0.wireOp",EDGE,"E11"),sQuery(id+"F0.wireOp",EDGE,"E12"),sQuery(id+"F0.wireOp",EDGE,"E13"),sQuery(id+"F0.wireOp",EDGE,"E14"),sQuery(id+"F0.wireOp",EDGE,"E15"),sQuery(id+"F0.wireOp",EDGE,"E16"),sQuery(id+"F0.wireOp",EDGE,"E17"),sQuery(id+"F0.wireOp",EDGE,"E18"),sQuery(id+"F0.wireOp",EDGE,"E21"),sQuery(id+"F0.wireOp",EDGE,"E22"),sQuery(id+"F0.wireOp",EDGE,"E24"),sQuery(id+"F0.wireOp",EDGE,"E25"),sQuery(id+"F0.wireOp",EDGE,"E26"),sQuery(id+"F0.wireOp",EDGE,"E27"),sQuery(id+"F0.wireOp",EDGE,"E29"),sQuery(id+"F0.wireOp",EDGE,"E30"),sQuery(id+"F0.wireOp",EDGE,"E31"),sQuery(id+"F0.wireOp",EDGE,"E32"),sQuery(id+"F0.wireOp",EDGE,"E34.filletArc"),sQuery(id+"F0.wireOp",EDGE,"E35.filletArc")])],"isStart":true});
            var sketch = newSketch(context, id + "F20", { "sketchPlane" : qUnion([Q0])});
            skLineSegment(sketch, "E107", {"start": v(-94.36, -211.94) * mm, "end": v(-101.68, -228.39) * mm});
            skLineSegment(sketch, "E108", {"start": v(-185.1, -168.05) * mm, "end": v(-171.72, -156) * mm});
            skLineSegment(sketch, "E109", {"start": v(-1.04, -250) * mm, "end": v(-1.04, -232) * mm});
            skPoint(sketch, "E110", {"position": v(-1.04, -238) * mm});
            skPoint(sketch, "E111", {"position": v(-96.8, -217.42) * mm});
            skPoint(sketch, "E112", {"position": v(-176.18, -160.02) * mm});
            skSolve(sketch);
        }
        {
            var Q0;
            Q0=sQuery(id+"F20.wireOp",VERTEX,"E112");
            var Q1;
            Q1=sQuery(id+"F20.wireOp",VERTEX,"E111");
            var Q2;
            Q2=sQuery(id+"F20.wireOp",VERTEX,"E110");
            var Q3;
            Q3=makeQuery(id+"F1.opExtrude","SWEPT_BODY",BODY,{"disambiguationData":[OSD([sQuery(id+"F0.wireOp",EDGE,"E9"),sQuery(id+"F0.wireOp",EDGE,"E10"),sQuery(id+"F0.wireOp",EDGE,"E11"),sQuery(id+"F0.wireOp",EDGE,"E12"),sQuery(id+"F0.wireOp",EDGE,"E13"),sQuery(id+"F0.wireOp",EDGE,"E14"),sQuery(id+"F0.wireOp",EDGE,"E15"),sQuery(id+"F0.wireOp",EDGE,"E16"),sQuery(id+"F0.wireOp",EDGE,"E17"),sQuery(id+"F0.wireOp",EDGE,"E18"),sQuery(id+"F0.wireOp",EDGE,"E21"),sQuery(id+"F0.wireOp",EDGE,"E22"),sQuery(id+"F0.wireOp",EDGE,"E24"),sQuery(id+"F0.wireOp",EDGE,"E25"),sQuery(id+"F0.wireOp",EDGE,"E26"),sQuery(id+"F0.wireOp",EDGE,"E27"),sQuery(id+"F0.wireOp",EDGE,"E29"),sQuery(id+"F0.wireOp",EDGE,"E30"),sQuery(id+"F0.wireOp",EDGE,"E31"),sQuery(id+"F0.wireOp",EDGE,"E32"),sQuery(id+"F0.wireOp",EDGE,"E34.filletArc"),sQuery(id+"F0.wireOp",EDGE,"E35.filletArc")])]});
            hole(context, id + "F21", {"style" : HoleStyle.SIMPLE, "endStyle" : HoleEndStyle.BLIND, "standardTappedOrClearance" : lookupTablePath({ "standard" : "ANSI", "engagement" : "75%", "pitch" : "32 tpi", "size" : "#8", "type" : "Tapped" }), "standardBlindInLast" : lookupTablePath({ "standard" : "ANSI", "engagement" : "75%", "pitch" : "32 tpi", "size" : "#8", "type" : "Tapped" }), "holeDiameter" : 3.45 * mm, "majorDiameter" : 4.17 * mm, "showTappedDepth" : true, "holeDepth" : 14.38 * mm, "isTappedThrough" : true, "tappedDepth" : 12 * mm, "tapClearance" : 3, "locations" : qUnion([Q0, Q1, Q2]), "scope" : qUnion([Q3])});
        }
        {
            var Q0;
            {var subQ3=sQuery(id+"F0.wireOp",EDGE,"E31");var subQ4=sQuery(id+"F0.wireOp",EDGE,"E30");var subQ5=sQuery(id+"F0.wireOp",EDGE,"E29");Q0=makeQuery(id+"F19.boolean.opBoolean","SPLIT",FACE,{"disambiguationData":[TD([makeQuery(id+"F1.opExtrude","SWEPT_FACE",FACE,{"disambiguationData":[OSD([subQ4])]})])],"derivedFrom":makeQuery(id+"F1.opExtrude","SWEPT_FACE",FACE,{"disambiguationData":[OSD([subQ5,subQ3])]})});}
            var sketch = newSketch(context, id + "F22", { "sketchPlane" : qUnion([Q0])});
            skLineSegment(sketch, "E113", {"start": v(10, -4.3) * mm, "end": v(16.5, -4.3) * mm});
            skLineSegment(sketch, "E114", {"start": v(10, -20.7) * mm, "end": v(16.5, -20.7) * mm});
            skLineSegment(sketch, "E115", {"start": v(-10, -4.3) * mm, "end": v(-27.61, -4.3) * mm});
            skLineSegment(sketch, "E116", {"start": v(-10, -20.7) * mm, "end": v(-27.61, -20.7) * mm});
            skPoint(sketch, "E117", {"position": v(13.25, -4.3) * mm});
            skPoint(sketch, "E118", {"position": v(13.25, -20.7) * mm});
            skPoint(sketch, "E119", {"position": v(-18.56, -4.3) * mm});
            skPoint(sketch, "E120", {"position": v(-18.56, -20.7) * mm});
            skSolve(sketch);
        }
        {
            var Q0;
            Q0=sQuery(id+"F22.wireOp",VERTEX,"960df98d-92ac-47f4-9385-bcb4d4738518");
            var Q1;
            Q1=sQuery(id+"F22.wireOp",VERTEX,"E117");
            var Q2;
            Q2=sQuery(id+"F22.wireOp",VERTEX,"E118");
            var Q3;
            Q3=sQuery(id+"F22.wireOp",VERTEX,"70c8c2b4-ec63-4f9a-a490-eeb2e280e894");
            var Q4;
            Q4=sQuery(id+"F22.wireOp",VERTEX,"E119");
            var Q5;
            Q5=sQuery(id+"F22.wireOp",VERTEX,"E120");
            var Q6;
            Q6=makeQuery(id+"F1.opExtrude","SWEPT_BODY",BODY,{"disambiguationData":[OSD([sQuery(id+"F0.wireOp",EDGE,"E9"),sQuery(id+"F0.wireOp",EDGE,"E10"),sQuery(id+"F0.wireOp",EDGE,"E11"),sQuery(id+"F0.wireOp",EDGE,"E12"),sQuery(id+"F0.wireOp",EDGE,"E13"),sQuery(id+"F0.wireOp",EDGE,"E14"),sQuery(id+"F0.wireOp",EDGE,"E15"),sQuery(id+"F0.wireOp",EDGE,"E16"),sQuery(id+"F0.wireOp",EDGE,"E17"),sQuery(id+"F0.wireOp",EDGE,"E18"),sQuery(id+"F0.wireOp",EDGE,"E21"),sQuery(id+"F0.wireOp",EDGE,"E22"),sQuery(id+"F0.wireOp",EDGE,"E24"),sQuery(id+"F0.wireOp",EDGE,"E25"),sQuery(id+"F0.wireOp",EDGE,"E26"),sQuery(id+"F0.wireOp",EDGE,"E27"),sQuery(id+"F0.wireOp",EDGE,"E29"),sQuery(id+"F0.wireOp",EDGE,"E30"),sQuery(id+"F0.wireOp",EDGE,"E31"),sQuery(id+"F0.wireOp",EDGE,"E32"),sQuery(id+"F0.wireOp",EDGE,"E34.filletArc"),sQuery(id+"F0.wireOp",EDGE,"E35.filletArc")])]});
            hole(context, id + "F23", {"style" : HoleStyle.SIMPLE, "endStyle" : HoleEndStyle.BLIND, "standardTappedOrClearance" : lookupTablePath({ "standard" : "ISO", "engagement" : "75%", "pitch" : "0.8 mm", "size" : "M5", "type" : "Tapped" }), "standardBlindInLast" : lookupTablePath({ "standard" : "ISO", "engagement" : "75%", "pitch" : "0.8 mm", "size" : "M5", "type" : "Tapped" }), "holeDiameter" : 4.2 * mm, "majorDiameter" : 5 * mm, "showTappedDepth" : true, "holeDepth" : 10 * mm, "isTappedThrough" : true, "tappedDepth" : 7.6 * mm, "tapClearance" : 3, "locations" : qUnion([Q0, Q1, Q2, Q3, Q4, Q5]), "scope" : qUnion([Q6])});
        }
        {
            var Q0;
            Q0=makeQuery(id+"F11.boolean.opBoolean","COPY",EDGE,{"derivedFrom":makeQuery(id+"F11.opExtrude","CAP_EDGE",EDGE,{"disambiguationData":[OSD([sQuery(id+"F10.wireOp",EDGE,"E62.left")])],"isStart":false})});
            var Q1;
            Q1=makeQuery(id+"F11.boolean.opBoolean","COPY",EDGE,{"derivedFrom":makeQuery(id+"F11.opExtrude","CAP_EDGE",EDGE,{"disambiguationData":[OSD([sQuery(id+"F10.wireOp",EDGE,"E62.top")])],"isStart":false})});
            var Q2;
            Q2=makeQuery(id+"F11.boolean.opBoolean","COPY",EDGE,{"derivedFrom":makeQuery(id+"F11.opExtrude","CAP_EDGE",EDGE,{"disambiguationData":[OSD([sQuery(id+"F10.wireOp",EDGE,"E62.right")])],"isStart":false})});
            var Q3;
            Q3=makeQuery(id+"F11.boolean.opBoolean","COPY",EDGE,{"derivedFrom":makeQuery(id+"F11.opExtrude","CAP_EDGE",EDGE,{"disambiguationData":[OSD([sQuery(id+"F10.wireOp",EDGE,"E62.bottom")])],"isStart":false})});
            var Q4;
            Q4=makeQuery(id+"F11.boolean.opBoolean","COPY",EDGE,{"derivedFrom":makeQuery(id+"F11.opExtrude","SWEPT_EDGE",EDGE,{"disambiguationData":[OSD([sQuery(id+"F10.wireOp",EDGE,"E62.top"),sQuery(id+"F10.wireOp",EDGE,"E62.left")])]})});
            var Q5;
            Q5=makeQuery(id+"F11.boolean.opBoolean","COPY",EDGE,{"derivedFrom":makeQuery(id+"F11.opExtrude","SWEPT_EDGE",EDGE,{"disambiguationData":[OSD([sQuery(id+"F10.wireOp",EDGE,"E62.top"),sQuery(id+"F10.wireOp",EDGE,"E62.right")])]})});
            var Q6;
            Q6=makeQuery(id+"F11.boolean.opBoolean","COPY",EDGE,{"derivedFrom":makeQuery(id+"F11.opExtrude","SWEPT_EDGE",EDGE,{"disambiguationData":[OSD([sQuery(id+"F10.wireOp",EDGE,"E62.bottom"),sQuery(id+"F10.wireOp",EDGE,"E62.right")])]})});
            fillet(context, id + "F24", {"entities" : qUnion([Q0, Q1, Q2, Q3, Q4, Q5, Q6]), "radius" : 0.5 * mm, "tangentPropagation" : true, "allowEdgeOverflow" : false});
        }
        {
            var Q0;
            Q0=makeQuery(id+"F3.boolean.opBoolean","COPY",EDGE,{"derivedFrom":makeQuery(id+"F3.opExtrude","CAP_EDGE",EDGE,{"disambiguationData":[OSD([sQuery(id+"F2.wireOp",EDGE,"E37.top")])],"isStart":false})});
            var Q1;
            Q1=makeQuery(id+"F3.boolean.opBoolean","COPY",EDGE,{"derivedFrom":makeQuery(id+"F3.opExtrude","CAP_EDGE",EDGE,{"disambiguationData":[OSD([sQuery(id+"F2.wireOp",EDGE,"E37.right")])],"isStart":false})});
            var Q2;
            Q2=makeQuery(id+"F3.boolean.opBoolean","COPY",EDGE,{"derivedFrom":makeQuery(id+"F3.opExtrude","SWEPT_EDGE",EDGE,{"disambiguationData":[OSD([sQuery(id+"F2.wireOp",EDGE,"E37.top"),sQuery(id+"F2.wireOp",EDGE,"E37.right")])]})});
            var Q3;
            Q3=makeQuery(id+"F3.boolean.opBoolean","COPY",EDGE,{"derivedFrom":makeQuery(id+"F3.opExtrude","SWEPT_EDGE",EDGE,{"disambiguationData":[OSD([sQuery(id+"F2.wireOp",EDGE,"E37.bottom"),sQuery(id+"F2.wireOp",EDGE,"E37.right")])]})});
            var Q4;
            Q4=makeQuery(id+"F3.boolean.opBoolean","COPY",EDGE,{"derivedFrom":makeQuery(id+"F3.opExtrude","CAP_EDGE",EDGE,{"disambiguationData":[OSD([sQuery(id+"F2.wireOp",EDGE,"E37.bottom")])],"isStart":false})});
            var Q5;
            Q5=makeQuery(id+"F3.boolean.opBoolean","COPY",EDGE,{"derivedFrom":makeQuery(id+"F3.opExtrude","CAP_EDGE",EDGE,{"disambiguationData":[OSD([sQuery(id+"F2.wireOp",EDGE,"E37.left")])],"isStart":false})});
            var Q6;
            Q6=makeQuery(id+"F3.boolean.opBoolean","COPY",EDGE,{"derivedFrom":makeQuery(id+"F3.opExtrude","SWEPT_EDGE",EDGE,{"disambiguationData":[OSD([sQuery(id+"F2.wireOp",EDGE,"E37.top"),sQuery(id+"F2.wireOp",EDGE,"E37.left")])]})});
            var Q7;
            Q7=makeQuery(id+"F3.boolean.opBoolean","COPY",EDGE,{"derivedFrom":makeQuery(id+"F3.opExtrude","SWEPT_EDGE",EDGE,{"disambiguationData":[OSD([sQuery(id+"F2.wireOp",EDGE,"E37.bottom"),sQuery(id+"F2.wireOp",EDGE,"E37.left")])]})});
            fillet(context, id + "F25", {"entities" : qUnion([Q0, Q1, Q2, Q3, Q4, Q5, Q6, Q7]), "radius" : 0.5 * mm, "tangentPropagation" : true, "allowEdgeOverflow" : false});
        }
        {
            var Q0;
            Q0=makeQuery(id+"F5.boolean.opBoolean","COPY",EDGE,{"derivedFrom":makeQuery(id+"F5.opExtrude","CAP_EDGE",EDGE,{"disambiguationData":[OSD([sQuery(id+"F4.wireOp",EDGE,"E39.bottom")])],"isStart":false})});
            var Q1;
            Q1=makeQuery(id+"F5.boolean.opBoolean","COPY",EDGE,{"derivedFrom":makeQuery(id+"F5.opExtrude","CAP_EDGE",EDGE,{"disambiguationData":[OSD([sQuery(id+"F4.wireOp",EDGE,"E39.top")])],"isStart":false})});
            var Q2;
            Q2=makeQuery(id+"F5.boolean.opBoolean","COPY",EDGE,{"derivedFrom":makeQuery(id+"F5.opExtrude","CAP_EDGE",EDGE,{"disambiguationData":[OSD([sQuery(id+"F4.wireOp",EDGE,"E39.right")])],"isStart":false})});
            var Q3;
            Q3=makeQuery(id+"F5.boolean.opBoolean","COPY",EDGE,{"derivedFrom":makeQuery(id+"F5.opExtrude","SWEPT_EDGE",EDGE,{"disambiguationData":[OSD([sQuery(id+"F4.wireOp",EDGE,"E39.top"),sQuery(id+"F4.wireOp",EDGE,"E39.right")])]})});
            var Q4;
            Q4=makeQuery(id+"F5.boolean.opBoolean","COPY",EDGE,{"derivedFrom":makeQuery(id+"F5.opExtrude","SWEPT_EDGE",EDGE,{"disambiguationData":[OSD([sQuery(id+"F4.wireOp",EDGE,"E39.bottom"),sQuery(id+"F4.wireOp",EDGE,"E39.right")])]})});
            var Q5;
            Q5=makeQuery(id+"F5.boolean.opBoolean","COPY",EDGE,{"derivedFrom":makeQuery(id+"F5.opExtrude","CAP_EDGE",EDGE,{"disambiguationData":[OSD([sQuery(id+"F4.wireOp",EDGE,"E39.left")])],"isStart":false})});
            var Q6;
            Q6=makeQuery(id+"F5.boolean.opBoolean","COPY",EDGE,{"derivedFrom":makeQuery(id+"F5.opExtrude","SWEPT_EDGE",EDGE,{"disambiguationData":[OSD([sQuery(id+"F4.wireOp",EDGE,"E39.top"),sQuery(id+"F4.wireOp",EDGE,"E39.left")])]})});
            var Q7;
            Q7=makeQuery(id+"F5.boolean.opBoolean","COPY",EDGE,{"derivedFrom":makeQuery(id+"F5.opExtrude","SWEPT_EDGE",EDGE,{"disambiguationData":[OSD([sQuery(id+"F4.wireOp",EDGE,"E39.bottom"),sQuery(id+"F4.wireOp",EDGE,"E39.left")])]})});
            fillet(context, id + "F26", {"entities" : qUnion([Q0, Q1, Q2, Q3, Q4, Q5, Q6, Q7]), "radius" : 0.5 * mm, "tangentPropagation" : true, "allowEdgeOverflow" : false});
        }
        {
            var Q0;
            {var subQ6=sQuery(id+"F0.wireOp",EDGE,"E27");var subQ7=sQuery(id+"F0.wireOp",EDGE,"E26");var subQ9=sQuery(id+"F0.wireOp",EDGE,"E24");Q0=makeQuery(id+"F15.boolean.opBoolean","SPLIT",FACE,{"disambiguationData":[TD([makeQuery(id+"F1.opExtrude","SWEPT_FACE",FACE,{"disambiguationData":[OSD([subQ7])]})])],"derivedFrom":makeQuery(id+"F1.opExtrude","SWEPT_FACE",FACE,{"disambiguationData":[OSD([subQ9,subQ6])]})});}
            var sketch = newSketch(context, id + "F27", { "sketchPlane" : qUnion([Q0])});
            skLineSegment(sketch, "E121", {"start": v(-10, -4.3) * mm, "end": v(-16, -4.3) * mm});
            skPoint(sketch, "E122", {"position": v(-13, -4.3) * mm});
            skLineSegment(sketch, "E123", {"start": v(-10, -20.7) * mm, "end": v(-16, -20.7) * mm});
            skPoint(sketch, "E124", {"position": v(-13, -20.7) * mm});
            skLineSegment(sketch, "E125", {"start": v(10, -4.3) * mm, "end": v(16, -4.3) * mm});
            skLineSegment(sketch, "E126", {"start": v(10, -20.7) * mm, "end": v(16, -20.7) * mm});
            skPoint(sketch, "E127", {"position": v(13, -4.3) * mm});
            skPoint(sketch, "E128", {"position": v(13, -20.7) * mm});
            skSolve(sketch);
        }
        {
            var Q0;
            Q0=sQuery(id+"F27.wireOp",VERTEX,"E122");
            var Q1;
            Q1=sQuery(id+"F27.wireOp",VERTEX,"E124");
            var Q2;
            Q2=sQuery(id+"F27.wireOp",VERTEX,"E127");
            var Q3;
            Q3=sQuery(id+"F27.wireOp",VERTEX,"E128");
            var Q4;
            Q4=makeQuery(id+"F1.opExtrude","SWEPT_BODY",BODY,{"disambiguationData":[OSD([sQuery(id+"F0.wireOp",EDGE,"E9"),sQuery(id+"F0.wireOp",EDGE,"E10"),sQuery(id+"F0.wireOp",EDGE,"E11"),sQuery(id+"F0.wireOp",EDGE,"E12"),sQuery(id+"F0.wireOp",EDGE,"E13"),sQuery(id+"F0.wireOp",EDGE,"E14"),sQuery(id+"F0.wireOp",EDGE,"E15"),sQuery(id+"F0.wireOp",EDGE,"E16"),sQuery(id+"F0.wireOp",EDGE,"E17"),sQuery(id+"F0.wireOp",EDGE,"E18"),sQuery(id+"F0.wireOp",EDGE,"E21"),sQuery(id+"F0.wireOp",EDGE,"E22"),sQuery(id+"F0.wireOp",EDGE,"E24"),sQuery(id+"F0.wireOp",EDGE,"E25"),sQuery(id+"F0.wireOp",EDGE,"E26"),sQuery(id+"F0.wireOp",EDGE,"E27"),sQuery(id+"F0.wireOp",EDGE,"E29"),sQuery(id+"F0.wireOp",EDGE,"E30"),sQuery(id+"F0.wireOp",EDGE,"E31"),sQuery(id+"F0.wireOp",EDGE,"E32"),sQuery(id+"F0.wireOp",EDGE,"E34.filletArc"),sQuery(id+"F0.wireOp",EDGE,"E35.filletArc")])]});
            hole(context, id + "F28", {"style" : HoleStyle.SIMPLE, "endStyle" : HoleEndStyle.BLIND, "standardTappedOrClearance" : lookupTablePath({ "standard" : "ISO", "engagement" : "75%", "pitch" : "0.8 mm", "size" : "M5", "type" : "Tapped" }), "standardBlindInLast" : lookupTablePath({ "standard" : "ISO", "engagement" : "75%", "pitch" : "0.8 mm", "size" : "M5", "type" : "Tapped" }), "holeDiameter" : 4.2 * mm, "majorDiameter" : 5 * mm, "showTappedDepth" : true, "holeDepth" : 10 * mm, "isTappedThrough" : true, "tappedDepth" : 7.6 * mm, "tapClearance" : 3, "locations" : qUnion([Q0, Q1, Q2, Q3]), "scope" : qUnion([Q4])});
        }
        {
            var Q0;
            {var subQ0=sQuery(id+"F0.wireOp",EDGE,"E22");var subQ9=sQuery(id+"F0.wireOp",EDGE,"E25");var subQ11=sQuery(id+"F0.wireOp",EDGE,"E21");Q0=makeQuery(id+"F17.boolean.opBoolean","SPLIT",FACE,{"disambiguationData":[TD([makeQuery(id+"F1.opExtrude","SWEPT_FACE",FACE,{"disambiguationData":[OSD([subQ0])]})])],"derivedFrom":makeQuery(id+"F1.opExtrude","SWEPT_FACE",FACE,{"disambiguationData":[OSD([subQ11,subQ9])]})});}
            var sketch = newSketch(context, id + "F29", { "sketchPlane" : qUnion([Q0])});
            skLineSegment(sketch, "E129", {"start": v(-10, -4.3) * mm, "end": v(-16, -4.3) * mm});
            skLineSegment(sketch, "E130", {"start": v(-10, -20.7) * mm, "end": v(-16, -20.7) * mm});
            skLineSegment(sketch, "E131", {"start": v(10, -4.3) * mm, "end": v(28.1, -4.3) * mm});
            skLineSegment(sketch, "E132", {"start": v(10, -20.7) * mm, "end": v(28.1, -20.7) * mm});
            skPoint(sketch, "E133", {"position": v(-13, -4.3) * mm});
            skPoint(sketch, "E134", {"position": v(-13, -20.7) * mm});
            skPoint(sketch, "E135", {"position": v(19.06, -4.3) * mm});
            skPoint(sketch, "E136", {"position": v(19.06, -20.7) * mm});
            skSolve(sketch);
        }
        {
            var Q0;
            Q0=sQuery(id+"F29.wireOp",VERTEX,"E133");
            var Q1;
            Q1=sQuery(id+"F29.wireOp",VERTEX,"E134");
            var Q2;
            Q2=sQuery(id+"F29.wireOp",VERTEX,"95fecb40-6dee-438e-ade6-2e9aa052387a");
            var Q3;
            Q3=sQuery(id+"F29.wireOp",VERTEX,"5c4d115d-a3d0-4a2b-9813-a859292176f2");
            var Q4;
            Q4=sQuery(id+"F29.wireOp",VERTEX,"E135");
            var Q5;
            Q5=sQuery(id+"F29.wireOp",VERTEX,"E136");
            var Q6;
            Q6=makeQuery(id+"F1.opExtrude","SWEPT_BODY",BODY,{"disambiguationData":[OSD([sQuery(id+"F0.wireOp",EDGE,"E9"),sQuery(id+"F0.wireOp",EDGE,"E10"),sQuery(id+"F0.wireOp",EDGE,"E11"),sQuery(id+"F0.wireOp",EDGE,"E12"),sQuery(id+"F0.wireOp",EDGE,"E13"),sQuery(id+"F0.wireOp",EDGE,"E14"),sQuery(id+"F0.wireOp",EDGE,"E15"),sQuery(id+"F0.wireOp",EDGE,"E16"),sQuery(id+"F0.wireOp",EDGE,"E17"),sQuery(id+"F0.wireOp",EDGE,"E18"),sQuery(id+"F0.wireOp",EDGE,"E21"),sQuery(id+"F0.wireOp",EDGE,"E22"),sQuery(id+"F0.wireOp",EDGE,"E24"),sQuery(id+"F0.wireOp",EDGE,"E25"),sQuery(id+"F0.wireOp",EDGE,"E26"),sQuery(id+"F0.wireOp",EDGE,"E27"),sQuery(id+"F0.wireOp",EDGE,"E29"),sQuery(id+"F0.wireOp",EDGE,"E30"),sQuery(id+"F0.wireOp",EDGE,"E31"),sQuery(id+"F0.wireOp",EDGE,"E32"),sQuery(id+"F0.wireOp",EDGE,"E34.filletArc"),sQuery(id+"F0.wireOp",EDGE,"E35.filletArc")])]});
            hole(context, id + "F30", {"style" : HoleStyle.SIMPLE, "endStyle" : HoleEndStyle.BLIND, "standardTappedOrClearance" : lookupTablePath({ "standard" : "ISO", "engagement" : "75%", "pitch" : "0.8 mm", "size" : "M5", "type" : "Tapped" }), "standardBlindInLast" : lookupTablePath({ "standard" : "ISO", "engagement" : "75%", "pitch" : "0.8 mm", "size" : "M5", "type" : "Tapped" }), "holeDiameter" : 4.2 * mm, "majorDiameter" : 5 * mm, "showTappedDepth" : true, "holeDepth" : 10 * mm, "isTappedThrough" : true, "tappedDepth" : 7.6 * mm, "tapClearance" : 3, "locations" : qUnion([Q0, Q1, Q2, Q3, Q4, Q5]), "scope" : qUnion([Q6])});
        }
        {
            var Q0;
            Q0=makeQuery(id+"F1.opExtrude","SWEPT_FACE",FACE,{"disambiguationData":[OSD([sQuery(id+"F0.wireOp",EDGE,"E32")])]});
            var sketch = newSketch(context, id + "F31", { "sketchPlane" : qUnion([Q0])});
            skLineSegment(sketch, "E137", {"start": v(-32.47, 0) * mm, "end": v(32.22, -25) * mm});
            skLineSegment(sketch, "E138", {"start": v(-32.47, -25) * mm, "end": v(32.22, 0) * mm});
            skPoint(sketch, "E139", {"position": v(-23.14, -21.4) * mm});
            skPoint(sketch, "E140", {"position": v(-23.14, -3.6) * mm});
            skPoint(sketch, "E141", {"position": v(32.22, -25) * mm});
            skSolve(sketch);
        }
        {
            var Q0;
            Q0=sQuery(id+"F31.wireOp",VERTEX,"E140");
            var Q1;
            Q1=sQuery(id+"F31.wireOp",VERTEX,"E139");
            var Q2;
            Q2=sQuery(id+"F31.wireOp",VERTEX,"c15fa140-9604-4616-bb4b-56b4743ac27f");
            var Q3;
            Q3=sQuery(id+"F31.wireOp",VERTEX,"ee11ad6e-ffd4-4928-85d1-b1639c15d129");
            var Q4;
            Q4=makeQuery(id+"F1.opExtrude","SWEPT_BODY",BODY,{"disambiguationData":[OSD([sQuery(id+"F0.wireOp",EDGE,"E9"),sQuery(id+"F0.wireOp",EDGE,"E10"),sQuery(id+"F0.wireOp",EDGE,"E11"),sQuery(id+"F0.wireOp",EDGE,"E12"),sQuery(id+"F0.wireOp",EDGE,"E13"),sQuery(id+"F0.wireOp",EDGE,"E14"),sQuery(id+"F0.wireOp",EDGE,"E15"),sQuery(id+"F0.wireOp",EDGE,"E16"),sQuery(id+"F0.wireOp",EDGE,"E17"),sQuery(id+"F0.wireOp",EDGE,"E18"),sQuery(id+"F0.wireOp",EDGE,"E21"),sQuery(id+"F0.wireOp",EDGE,"E22"),sQuery(id+"F0.wireOp",EDGE,"E24"),sQuery(id+"F0.wireOp",EDGE,"E25"),sQuery(id+"F0.wireOp",EDGE,"E26"),sQuery(id+"F0.wireOp",EDGE,"E27"),sQuery(id+"F0.wireOp",EDGE,"E29"),sQuery(id+"F0.wireOp",EDGE,"E30"),sQuery(id+"F0.wireOp",EDGE,"E31"),sQuery(id+"F0.wireOp",EDGE,"E32"),sQuery(id+"F0.wireOp",EDGE,"E34.filletArc"),sQuery(id+"F0.wireOp",EDGE,"E35.filletArc")])]});
            hole(context, id + "F32", {"style" : HoleStyle.SIMPLE, "endStyle" : HoleEndStyle.BLIND, "holeDiameter" : 3.02 * mm, "majorDiameter" : 5 * mm, "holeDepth" : 6 * mm, "isTappedThrough" : true, "tappedDepth" : 7.6 * mm, "tapClearance" : 3, "locations" : qUnion([Q0, Q1, Q2, Q3]), "scope" : qUnion([Q4])});
        }
        {
            var Q0;
            Q0=makeQuery(id+"F1.opExtrude","SWEPT_FACE",FACE,{"disambiguationData":[OSD([sQuery(id+"F0.wireOp",EDGE,"E26")])]});
            var sketch = newSketch(context, id + "F33", { "sketchPlane" : qUnion([Q0])});
            skLineSegment(sketch, "E142", {"start": v(-32.59, 0) * mm, "end": v(32.59, -25) * mm});
            skLineSegment(sketch, "E143", {"start": v(-32.59, -25) * mm, "end": v(32.59, 0) * mm});
            skPoint(sketch, "E144", {"position": v(23.25, -3.58) * mm});
            skPoint(sketch, "E145", {"position": v(23.25, -21.42) * mm});
            skSolve(sketch);
        }
        {
            var Q0;
            Q0=sQuery(id+"F33.wireOp",VERTEX,"2f9b4e08-407a-4854-a18f-1e0d48b055ba");
            var Q1;
            Q1=sQuery(id+"F33.wireOp",VERTEX,"d0e48b6c-0c36-4a9f-8b0d-3dbf71a8332a");
            var Q2;
            Q2=sQuery(id+"F33.wireOp",VERTEX,"E144");
            var Q3;
            Q3=sQuery(id+"F33.wireOp",VERTEX,"E145");
            var Q4;
            Q4=makeQuery(id+"F1.opExtrude","SWEPT_BODY",BODY,{"disambiguationData":[OSD([sQuery(id+"F0.wireOp",EDGE,"E9"),sQuery(id+"F0.wireOp",EDGE,"E10"),sQuery(id+"F0.wireOp",EDGE,"E11"),sQuery(id+"F0.wireOp",EDGE,"E12"),sQuery(id+"F0.wireOp",EDGE,"E13"),sQuery(id+"F0.wireOp",EDGE,"E14"),sQuery(id+"F0.wireOp",EDGE,"E15"),sQuery(id+"F0.wireOp",EDGE,"E16"),sQuery(id+"F0.wireOp",EDGE,"E17"),sQuery(id+"F0.wireOp",EDGE,"E18"),sQuery(id+"F0.wireOp",EDGE,"E21"),sQuery(id+"F0.wireOp",EDGE,"E22"),sQuery(id+"F0.wireOp",EDGE,"E24"),sQuery(id+"F0.wireOp",EDGE,"E25"),sQuery(id+"F0.wireOp",EDGE,"E26"),sQuery(id+"F0.wireOp",EDGE,"E27"),sQuery(id+"F0.wireOp",EDGE,"E29"),sQuery(id+"F0.wireOp",EDGE,"E30"),sQuery(id+"F0.wireOp",EDGE,"E31"),sQuery(id+"F0.wireOp",EDGE,"E32"),sQuery(id+"F0.wireOp",EDGE,"E34.filletArc"),sQuery(id+"F0.wireOp",EDGE,"E35.filletArc")])]});
            hole(context, id + "F34", {"style" : HoleStyle.SIMPLE, "endStyle" : HoleEndStyle.BLIND, "holeDiameter" : 3.02 * mm, "majorDiameter" : 5 * mm, "holeDepth" : 6 * mm, "isTappedThrough" : true, "tappedDepth" : 7.6 * mm, "tapClearance" : 3, "locations" : qUnion([Q0, Q1, Q2, Q3]), "scope" : qUnion([Q4])});
        }
    });
